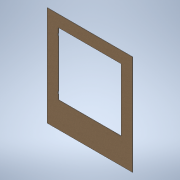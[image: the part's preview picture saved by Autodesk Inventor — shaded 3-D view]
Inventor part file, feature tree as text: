
AUTODESK INVENTOR PART (.ipt)
format: ipt  version: 2022 (Build 260153000, 153)  size: 158,208 bytes
history: native  units: mm
features: sketch x4, extrude x3, other x1, fillet x1, hole x1
ambient origin geometry x8: Origin, YZ Plane, XZ Plane, XY Plane, X Axis, Y Axis, Z Axis, Center Point
bodies: Body1 (feature_tree)
feature tree (10):
  other  "Sólido1"
  extrude  "Extrusão1"  Depth=700.0mm
  extrude  "Extrusão2"  Depth=80.0mm
  fillet  "Arredondamento1"  Radius=80.0mm
  hole  "Furo1"  [1 undecoded]
  extrude  "Extrusão3"  Depth=2.0mm
  sketch  "Esboço1"  dims[d0=600.0mm d1=700.0mm]
  sketch  "Esboço2"  dims[d2=3.0mm d3=0.0mm d4=80.0mm d5=80.0mm]
  sketch  "Esboço3"  dims[d6=80.0mm d7=180.0mm]
  sketch  "Esboço4"  dims[d8=10.0mm d9=0.0mm d10=2.0mm d11=2.0mm d12=6.0mm d13=4.0mm d14=2.0mm d15=90.0deg d16=8.0mm d17=20.594885mm d19=3.0mm d20=17.0mm d21=3.0mm d22=17.0mm d23=10.0mm d24=0.0mm]
note: 1 required parameter value undecoded (feature->parameter linkage not recoverable at this tier; creation-order binding heuristic only, values carry confidence <= 0.55)
